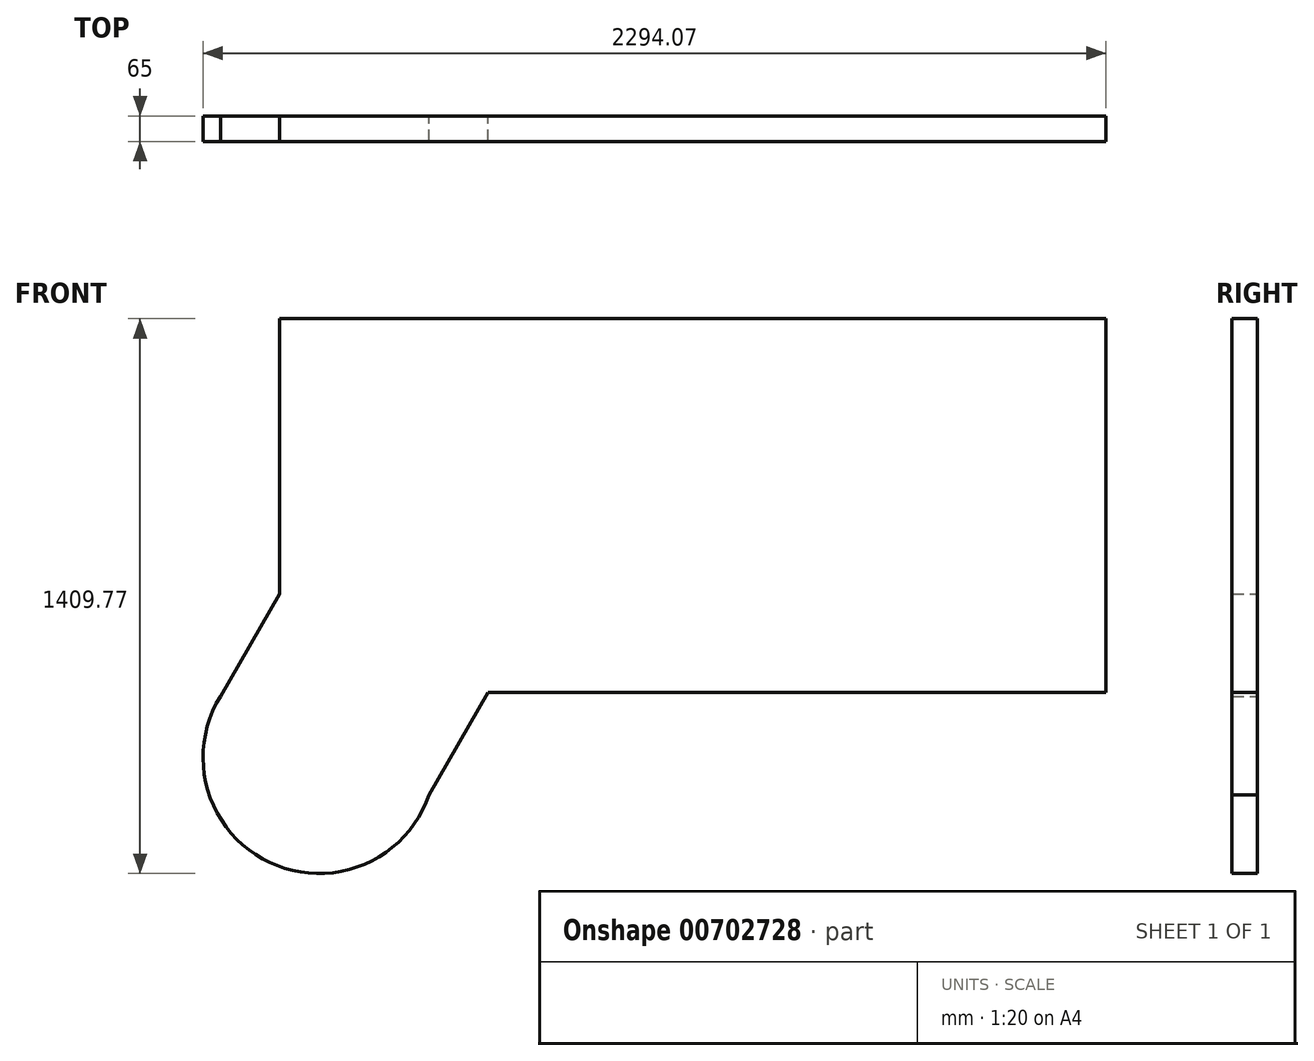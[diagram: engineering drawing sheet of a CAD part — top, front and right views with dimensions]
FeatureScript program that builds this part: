
annotation { "Feature Type Name" : "Feature", "Feature Type Description" : "" }
export const myFeature = defineFeature(function(context is Context, id is Id, definition is map)
    precondition{}
    {
        {
            var Q0;
            Q0=qCreatedBy(makeId("Front.planeOp"),FACE);
            var sketch = newSketch(context, id + "F0", { "sketchPlane" : qUnion([Q0])});
            skLineSegment(sketch, "E0", {"start": v(0, 0) * mm, "end": v(0, -700) * mm});
            skLineSegment(sketch, "E1", {"start": v(0, 0) * mm, "end": v(2100, 0) * mm});
            skLineSegment(sketch, "E2", {"start": v(2100, 0) * mm, "end": v(2100, -950) * mm});
            skLineSegment(sketch, "E3", {"start": v(2100, -950) * mm, "end": v(530, -950) * mm});
            skLineSegment(sketch, "E4", {"start": v(530, -950) * mm, "end": v(380, -1209.8) * mm});
            skLineSegment(sketch, "E5", {"start": v(0, -700) * mm, "end": v(-150, -959.8) * mm});
            skCircle(sketch, "E6", {"center": v(100.81, -1114.89) * mm, "radius": 294.88 * mm});
            skPoint(sketch, "E6.third.point", {"position": v(-150, -1269.96) * mm});
            skSolve(sketch);
        }
        {
            var Q0;
            {var subQ0=sQuery(id+"F0.wireOp",EDGE,"E6");var subQ1=makeQuery(id+"F0.imprint","INTERSECT",VERTEX,{"derivedFrom":[sQuery(id+"F0.wireOp",EDGE,"E4"),subQ0]});Q0=makeQuery(id+"F0.imprint","IMPRINT",FACE,{"disambiguationData":[TD([[makeQuery(id+"F0.imprint","IMPRINT",EDGE,{"disambiguationData":[TD([[subQ1,1.0]])],"derivedFrom":subQ0}),1.0]])]});}
            var Q1;
            Q1=makeQuery(id+"F0.imprint","IMPRINT",FACE,{"disambiguationData":[TD([[makeQuery(id+"F0.imprint","IMPRINT",EDGE,{"derivedFrom":sQuery(id+"F0.wireOp",EDGE,"E0")}),1.0]])]});
            extrude(context, id + "F1", {"entities" : qUnion([Q0, Q1]), "endBound" : BoundingType.SYMMETRIC, "depth" : 65 * mm, "offsetDistance" : 25 * mm});
        }
    });
